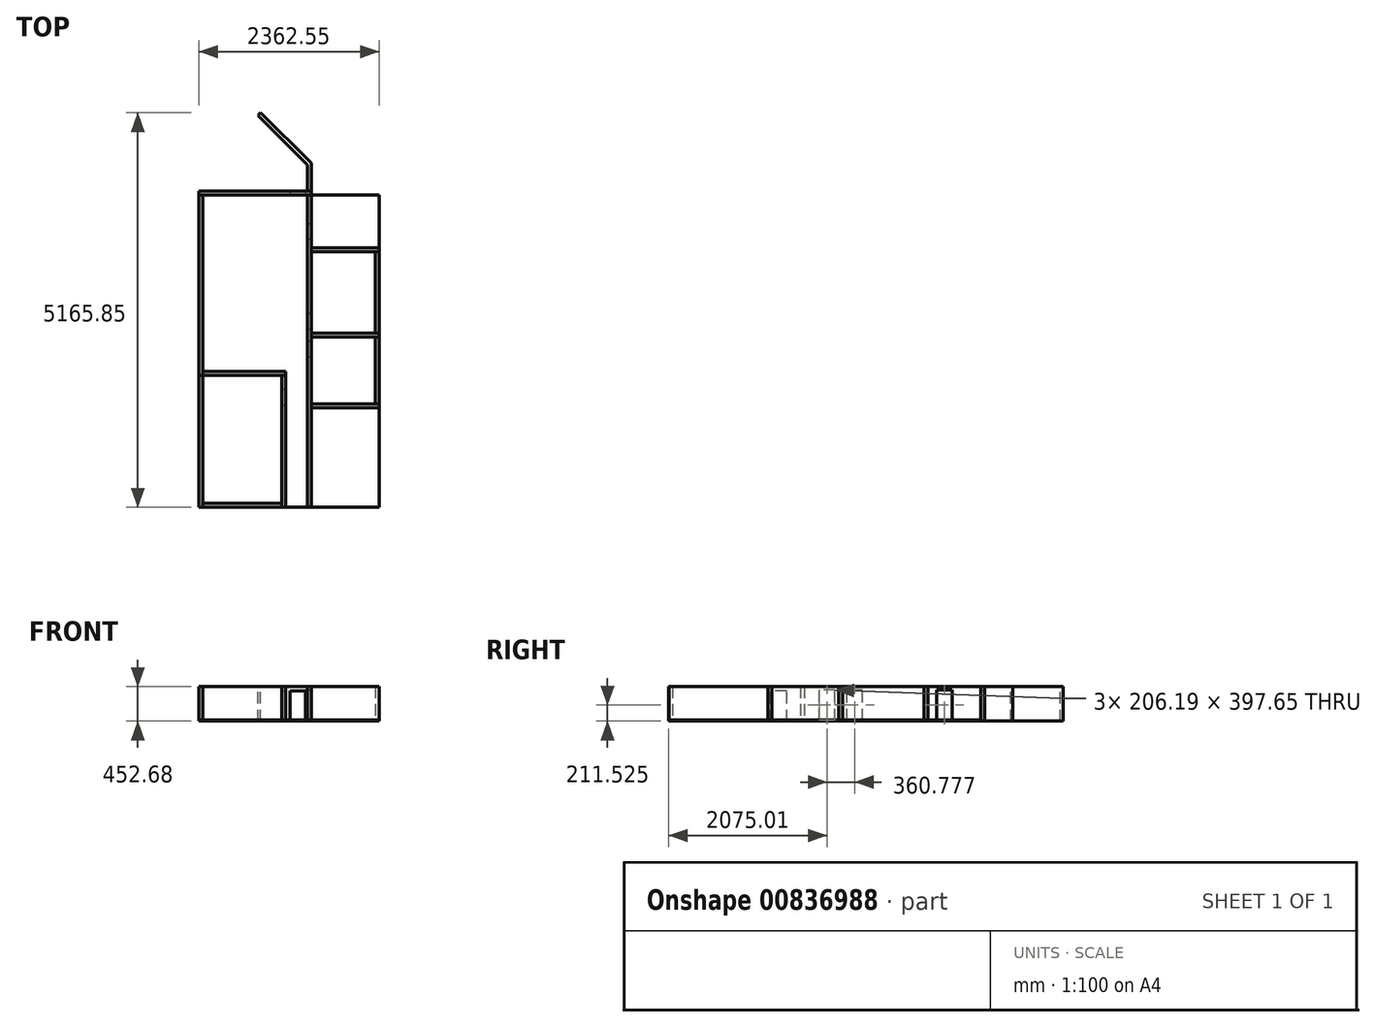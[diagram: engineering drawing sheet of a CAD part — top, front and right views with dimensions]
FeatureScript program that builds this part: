
annotation { "Feature Type Name" : "Feature", "Feature Type Description" : "" }
export const myFeature = defineFeature(function(context is Context, id is Id, definition is map)
    precondition{}
    {
        {
            var Q0;
            Q0=qCreatedBy(makeId("Front.planeOp"),FACE);
            var sketch = newSketch(context, id + "F0", { "sketchPlane" : qUnion([Q0])});
            skLineSegment(sketch, "E0.bottom", {"start": v(0, 0) * mm, "end": v(1473.55, 0) * mm});
            skLineSegment(sketch, "E0.top", {"start": v(0, 452.68) * mm, "end": v(1473.55, 452.68) * mm});
            skLineSegment(sketch, "E0.left", {"start": v(0, 0) * mm, "end": v(0, 452.68) * mm});
            skLineSegment(sketch, "E0.right", {"start": v(1473.55, 0) * mm, "end": v(1473.55, 452.68) * mm});
            skSolve(sketch);
        }
        {
            var Q0;
            Q0 = qSketchRegion(id + "F0", true);
            extrude(context, id + "F1", {"entities" : qUnion([Q0]), "depth" : 50.8 * mm, "offsetDistance" : 25.4 * mm});
        }
        {
            var Q0;
            Q0=makeQuery(id+"F1.opExtrude","CAP_FACE",FACE,{"disambiguationData":[OSD([sQuery(id+"F0.wireOp",EDGE,"E0.bottom"),sQuery(id+"F0.wireOp",EDGE,"E0.top"),sQuery(id+"F0.wireOp",EDGE,"E0.left"),sQuery(id+"F0.wireOp",EDGE,"E0.right")])],"isStart":false});
            var sketch = newSketch(context, id + "F2", { "sketchPlane" : qUnion([Q0])});
            skLineSegment(sketch, "E1.bottom", {"start": v(1397.99, 0) * mm, "end": v(1191.8, 0) * mm});
            skLineSegment(sketch, "E1.top", {"start": v(1397.99, 398.23) * mm, "end": v(1191.8, 398.23) * mm});
            skLineSegment(sketch, "E1.left", {"start": v(1397.99, 0) * mm, "end": v(1397.99, 398.23) * mm});
            skLineSegment(sketch, "E1.right", {"start": v(1191.8, 0) * mm, "end": v(1191.8, 398.23) * mm});
            skSolve(sketch);
        }
        {
            var Q0;
            Q0=makeQuery(id+"F2.imprint","IMPRINT",FACE,{"disambiguationData":[TD([[makeQuery(id+"F2.imprint","IMPRINT",EDGE,{"derivedFrom":sQuery(id+"F2.wireOp",EDGE,"E1.bottom")}),1.0]])]});
            extrude(context, id + "F3", {"entities" : qUnion([Q0]), "operationType" : NewBodyOperationType.REMOVE, "oppositeDirection" : true, "depth" : 71.12 * mm, "offsetDistance" : 25.4 * mm});
        }
        {
            var Q0;
            Q0=makeQuery(id+"F1.opExtrude","CAP_FACE",FACE,{"disambiguationData":[OSD([sQuery(id+"F0.wireOp",EDGE,"E0.bottom"),sQuery(id+"F0.wireOp",EDGE,"E0.top"),sQuery(id+"F0.wireOp",EDGE,"E0.left"),sQuery(id+"F0.wireOp",EDGE,"E0.right")])],"isStart":false});
            var sketch = newSketch(context, id + "F4", { "sketchPlane" : qUnion([Q0])});
            skLineSegment(sketch, "E2.bottom", {"start": v(0, 452.68) * mm, "end": v(50.8, 452.68) * mm});
            skLineSegment(sketch, "E2.top", {"start": v(0, 0) * mm, "end": v(50.8, 0) * mm});
            skLineSegment(sketch, "E2.left", {"start": v(0, 452.68) * mm, "end": v(0, 0) * mm});
            skLineSegment(sketch, "E2.right", {"start": v(50.8, 452.68) * mm, "end": v(50.8, 0) * mm});
            skSolve(sketch);
        }
        {
            var Q0;
            Q0=makeQuery(id+"F4.imprint","IMPRINT",FACE,{"disambiguationData":[TD([[makeQuery(id+"F4.imprint","IMPRINT",EDGE,{"derivedFrom":sQuery(id+"F4.wireOp",EDGE,"E2.bottom")}),-1.0]])]});
            extrude(context, id + "F5", {"entities" : qUnion([Q0]), "depth" : 2362.2 * mm, "offsetDistance" : 25.4 * mm});
        }
        {
            var Q0;
            Q0=makeQuery(id+"F5.opExtrude","SWEPT_FACE",FACE,{"disambiguationData":[OSD([sQuery(id+"F4.wireOp",EDGE,"E2.right")])]});
            var sketch = newSketch(context, id + "F6", { "sketchPlane" : qUnion([Q0])});
            skLineSegment(sketch, "E3.bottom", {"start": v(-2413, 452.68) * mm, "end": v(-2362.2, 452.68) * mm});
            skLineSegment(sketch, "E3.top", {"start": v(-2413, 0) * mm, "end": v(-2362.2, 0) * mm});
            skLineSegment(sketch, "E3.left", {"start": v(-2413, 452.68) * mm, "end": v(-2413, 0) * mm});
            skLineSegment(sketch, "E3.right", {"start": v(-2362.2, 452.68) * mm, "end": v(-2362.2, 0) * mm});
            skSolve(sketch);
        }
        {
            var Q0;
            Q0=makeQuery(id+"F6.imprint","IMPRINT",FACE,{"disambiguationData":[TD([[makeQuery(id+"F6.imprint","IMPRINT",EDGE,{"derivedFrom":sQuery(id+"F6.wireOp",EDGE,"E3.bottom")}),-1.0]])]});
            extrude(context, id + "F7", {"entities" : qUnion([Q0]), "depth" : 1084.58 * mm, "offsetDistance" : 25.4 * mm});
        }
        {
            var Q0;
            Q0=makeQuery(id+"F7.opExtrude","SWEPT_FACE",FACE,{"disambiguationData":[OSD([sQuery(id+"F6.wireOp",EDGE,"E3.left")])]});
            var sketch = newSketch(context, id + "F8", { "sketchPlane" : qUnion([Q0])});
            skLineSegment(sketch, "E4.bottom", {"start": v(1135.38, 452.68) * mm, "end": v(1084.58, 452.68) * mm});
            skLineSegment(sketch, "E4.top", {"start": v(1135.38, 0) * mm, "end": v(1084.58, 0) * mm});
            skLineSegment(sketch, "E4.left", {"start": v(1135.38, 452.68) * mm, "end": v(1135.38, 0) * mm});
            skLineSegment(sketch, "E4.right", {"start": v(1084.58, 452.68) * mm, "end": v(1084.58, 0) * mm});
            skSolve(sketch);
        }
        {
            var Q0;
            Q0=makeQuery(id+"F8.imprint","IMPRINT",FACE,{"disambiguationData":[TD([[makeQuery(id+"F8.imprint","IMPRINT",EDGE,{"derivedFrom":sQuery(id+"F8.wireOp",EDGE,"E4.bottom")}),1.0]])]});
            extrude(context, id + "F9", {"entities" : qUnion([Q0]), "depth" : 1727.2 * mm, "offsetDistance" : 25.4 * mm});
        }
        {
            var Q0;
            Q0=makeQuery(id+"F9.opExtrude","SWEPT_FACE",FACE,{"disambiguationData":[OSD([sQuery(id+"F8.wireOp",EDGE,"E4.left")])]});
            var sketch = newSketch(context, id + "F10", { "sketchPlane" : qUnion([Q0])});
            skLineSegment(sketch, "E5.bottom", {"start": v(-2593.9, 0) * mm, "end": v(-2800.09, 0) * mm});
            skLineSegment(sketch, "E5.top", {"start": v(-2593.9, 397.65) * mm, "end": v(-2800.09, 397.65) * mm});
            skLineSegment(sketch, "E5.left", {"start": v(-2593.9, 0) * mm, "end": v(-2593.9, 397.65) * mm});
            skLineSegment(sketch, "E5.right", {"start": v(-2800.09, 0) * mm, "end": v(-2800.09, 397.65) * mm});
            skSolve(sketch);
        }
        {
            var Q0;
            Q0=makeQuery(id+"F10.imprint","IMPRINT",FACE,{"disambiguationData":[TD([[makeQuery(id+"F10.imprint","IMPRINT",EDGE,{"derivedFrom":sQuery(id+"F10.wireOp",EDGE,"E5.bottom")}),1.0]])]});
            extrude(context, id + "F11", {"entities" : qUnion([Q0]), "operationType" : NewBodyOperationType.REMOVE, "oppositeDirection" : true, "depth" : 111.76 * mm, "offsetDistance" : 25.4 * mm});
        }
        {
            var Q0;
            Q0=makeQuery(id+"F1.opExtrude","CAP_FACE",FACE,{"disambiguationData":[OSD([sQuery(id+"F0.wireOp",EDGE,"E0.bottom"),sQuery(id+"F0.wireOp",EDGE,"E0.top"),sQuery(id+"F0.wireOp",EDGE,"E0.left"),sQuery(id+"F0.wireOp",EDGE,"E0.right")])],"isStart":false});
            var sketch = newSketch(context, id + "F12", { "sketchPlane" : qUnion([Q0])});
            skLineSegment(sketch, "E6.bottom", {"start": v(0, 0) * mm, "end": v(1473.55, 0) * mm});
            skLineSegment(sketch, "E6.top", {"start": v(0, 12.7) * mm, "end": v(1473.55, 12.7) * mm});
            skLineSegment(sketch, "E6.left", {"start": v(0, 0) * mm, "end": v(0, 12.7) * mm});
            skLineSegment(sketch, "E6.right", {"start": v(1473.55, 0) * mm, "end": v(1473.55, 12.7) * mm});
            skSolve(sketch);
        }
        {
            var Q0;
            {var subQ0=sQuery(id+"F12.wireOp",EDGE,"E6.left");Q0=makeQuery(id+"F12.imprint","IMPRINT",FACE,{"disambiguationData":[TD([[makeQuery(id+"F12.imprint","IMPRINT",EDGE,{"derivedFrom":subQ0}),-1.0]])]});}
            var Q1;
            {var subQ0=sQuery(id+"F12.wireOp",EDGE,"E6.bottom");var subQ1=makeQuery(id+"F3.boolean.opBoolean","COPY",EDGE,{"derivedFrom":makeQuery(id+"F3.opExtrude","CAP_EDGE",EDGE,{"disambiguationData":[OSD([sQuery(id+"F2.wireOp",EDGE,"E1.right")])],"isStart":true})});var subQ2=makeQuery(id+"F12.imprint","INTERSECT",VERTEX,{"derivedFrom":[subQ1,subQ0]});Q1=makeQuery(id+"F12.imprint","IMPRINT",FACE,{"disambiguationData":[TD([[makeQuery(id+"F12.imprint","IMPRINT",EDGE,{"disambiguationData":[TD([[subQ2,-1.0]])],"derivedFrom":subQ0}),1.0]])]});}
            var Q2;
            {var subQ0=sQuery(id+"F12.wireOp",EDGE,"E6.right");Q2=makeQuery(id+"F12.imprint","IMPRINT",FACE,{"disambiguationData":[TD([[makeQuery(id+"F12.imprint","IMPRINT",EDGE,{"derivedFrom":subQ0}),1.0]])]});}
            extrude(context, id + "F13", {"entities" : qUnion([Q0, Q1, Q2]), "depth" : 4089.4 * mm, "offsetDistance" : 25.4 * mm});
        }
        {
            var Q0;
            Q0=makeQuery(id+"F5.opExtrude","CAP_FACE",FACE,{"disambiguationData":[OSD([sQuery(id+"F4.wireOp",EDGE,"E2.bottom"),sQuery(id+"F4.wireOp",EDGE,"E2.top"),sQuery(id+"F4.wireOp",EDGE,"E2.left"),sQuery(id+"F4.wireOp",EDGE,"E2.right")])],"isStart":false});
            extrude(context, id + "F14", {"entities" : qUnion([Q0]), "depth" : 1727.2 * mm, "offsetDistance" : 25.4 * mm});
        }
        {
            var Q0;
            Q0=makeQuery(id+"F14.opExtrude","SWEPT_FACE",FACE,{"disambiguationData":[OSD([sQuery(id+"F4.wireOp",EDGE,"E2.right")])]});
            var sketch = newSketch(context, id + "F15", { "sketchPlane" : qUnion([Q0])});
            skLineSegment(sketch, "E7.bottom", {"start": v(-4140.2, 452.68) * mm, "end": v(-4089.4, 452.68) * mm});
            skLineSegment(sketch, "E7.top", {"start": v(-4140.2, 0) * mm, "end": v(-4089.4, 0) * mm});
            skLineSegment(sketch, "E7.left", {"start": v(-4140.2, 452.68) * mm, "end": v(-4140.2, 0) * mm});
            skLineSegment(sketch, "E7.right", {"start": v(-4089.4, 452.68) * mm, "end": v(-4089.4, 0) * mm});
            skSolve(sketch);
        }
        {
            var Q0;
            Q0=makeQuery(id+"F15.imprint","IMPRINT",FACE,{"disambiguationData":[TD([[makeQuery(id+"F15.imprint","IMPRINT",EDGE,{"derivedFrom":sQuery(id+"F15.wireOp",EDGE,"E7.bottom")}),-1.0]])]});
            extrude(context, id + "F16", {"entities" : qUnion([Q0]), "depth" : 1033.78 * mm, "offsetDistance" : 25.4 * mm});
        }
        {
            var Q0;
            Q0=makeQuery(id+"F1.opExtrude","CAP_FACE",FACE,{"disambiguationData":[OSD([sQuery(id+"F0.wireOp",EDGE,"E0.bottom"),sQuery(id+"F0.wireOp",EDGE,"E0.top"),sQuery(id+"F0.wireOp",EDGE,"E0.left"),sQuery(id+"F0.wireOp",EDGE,"E0.right")])],"isStart":false});
            var sketch = newSketch(context, id + "F17", { "sketchPlane" : qUnion([Q0])});
            skLineSegment(sketch, "E8.bottom", {"start": v(1473.55, 452.68) * mm, "end": v(1422.75, 452.68) * mm});
            skLineSegment(sketch, "E8.top", {"start": v(1473.55, 0) * mm, "end": v(1422.75, 0) * mm});
            skLineSegment(sketch, "E8.left", {"start": v(1473.55, 452.68) * mm, "end": v(1473.55, 0) * mm});
            skLineSegment(sketch, "E8.right", {"start": v(1422.75, 452.68) * mm, "end": v(1422.75, 0) * mm});
            skSolve(sketch);
        }
        {
            var Q0;
            Q0=makeQuery(id+"F17.imprint","IMPRINT",FACE,{"disambiguationData":[TD([[makeQuery(id+"F17.imprint","IMPRINT",EDGE,{"derivedFrom":sQuery(id+"F17.wireOp",EDGE,"E8.bottom")}),-1.0]])]});
            extrude(context, id + "F18", {"entities" : qUnion([Q0]), "depth" : 4081.78 * mm, "offsetDistance" : 25.4 * mm});
        }
        {
            var Q0;
            Q0=makeQuery(id+"F18.opExtrude","SWEPT_FACE",FACE,{"disambiguationData":[OSD([sQuery(id+"F17.wireOp",EDGE,"E8.left")])]});
            var sketch = newSketch(context, id + "F19", { "sketchPlane" : qUnion([Q0])});
            skLineSegment(sketch, "E9.bottom", {"start": v(-423.05, 12.7) * mm, "end": v(-629.23, 12.7) * mm});
            skLineSegment(sketch, "E9.top", {"start": v(-423.05, 410.35) * mm, "end": v(-629.23, 410.35) * mm});
            skLineSegment(sketch, "E9.left", {"start": v(-423.05, 12.7) * mm, "end": v(-423.05, 410.35) * mm});
            skLineSegment(sketch, "E9.right", {"start": v(-629.23, 12.7) * mm, "end": v(-629.23, 410.35) * mm});
            skLineSegment(sketch, "E10.bottom", {"start": v(-1601.32, 12.7) * mm, "end": v(-1807.5, 12.7) * mm});
            skLineSegment(sketch, "E10.top", {"start": v(-1601.32, 410.35) * mm, "end": v(-1807.5, 410.35) * mm});
            skLineSegment(sketch, "E10.left", {"start": v(-1601.32, 12.7) * mm, "end": v(-1601.32, 410.35) * mm});
            skLineSegment(sketch, "E10.right", {"start": v(-1807.5, 12.7) * mm, "end": v(-1807.5, 410.35) * mm});
            skLineSegment(sketch, "E11.bottom", {"start": v(-1962.1, 12.7) * mm, "end": v(-2168.29, 12.7) * mm});
            skLineSegment(sketch, "E11.top", {"start": v(-1962.1, 410.35) * mm, "end": v(-2168.29, 410.35) * mm});
            skLineSegment(sketch, "E11.left", {"start": v(-1962.1, 12.7) * mm, "end": v(-1962.1, 410.35) * mm});
            skLineSegment(sketch, "E11.right", {"start": v(-2168.29, 12.7) * mm, "end": v(-2168.29, 410.35) * mm});
            skSolve(sketch);
        }
        {
            var Q0;
            Q0=makeQuery(id+"F19.imprint","IMPRINT",FACE,{"disambiguationData":[TD([[makeQuery(id+"F19.imprint","IMPRINT",EDGE,{"derivedFrom":sQuery(id+"F19.wireOp",EDGE,"E11.bottom")}),-1.0]])]});
            var Q1;
            Q1=makeQuery(id+"F19.imprint","IMPRINT",FACE,{"disambiguationData":[TD([[makeQuery(id+"F19.imprint","IMPRINT",EDGE,{"derivedFrom":sQuery(id+"F19.wireOp",EDGE,"E10.bottom")}),-1.0]])]});
            var Q2;
            Q2=makeQuery(id+"F19.imprint","IMPRINT",FACE,{"disambiguationData":[TD([[makeQuery(id+"F19.imprint","IMPRINT",EDGE,{"derivedFrom":sQuery(id+"F19.wireOp",EDGE,"E9.bottom")}),-1.0]])]});
            extrude(context, id + "F20", {"entities" : qUnion([Q0, Q1, Q2]), "operationType" : NewBodyOperationType.REMOVE, "oppositeDirection" : true, "depth" : 314.96 * mm, "offsetDistance" : 25.4 * mm});
        }
        {
            var Q0;
            Q0=makeQuery(id+"F18.opExtrude","SWEPT_FACE",FACE,{"disambiguationData":[OSD([sQuery(id+"F17.wireOp",EDGE,"E8.left")])]});
            var sketch = newSketch(context, id + "F21", { "sketchPlane" : qUnion([Q0])});
            skLineSegment(sketch, "E12.bottom", {"start": v(-1910.2, 452.68) * mm, "end": v(-1859.4, 452.68) * mm});
            skLineSegment(sketch, "E12.top", {"start": v(-1910.2, 12.7) * mm, "end": v(-1859.4, 12.7) * mm});
            skLineSegment(sketch, "E12.left", {"start": v(-1910.2, 452.68) * mm, "end": v(-1910.2, 12.7) * mm});
            skLineSegment(sketch, "E12.right", {"start": v(-1859.4, 452.68) * mm, "end": v(-1859.4, 12.7) * mm});
            skSolve(sketch);
        }
        {
            var Q0;
            Q0=makeQuery(id+"F21.imprint","IMPRINT",FACE,{"disambiguationData":[TD([[makeQuery(id+"F21.imprint","IMPRINT",EDGE,{"derivedFrom":sQuery(id+"F21.wireOp",EDGE,"E12.bottom")}),-1.0]])]});
            extrude(context, id + "F22", {"entities" : qUnion([Q0]), "depth" : 889 * mm, "offsetDistance" : 25.4 * mm});
        }
        {
            var Q0;
            Q0=makeQuery(id+"F18.opExtrude","SWEPT_FACE",FACE,{"disambiguationData":[OSD([sQuery(id+"F17.wireOp",EDGE,"E8.left")])]});
            var sketch = newSketch(context, id + "F23", { "sketchPlane" : qUnion([Q0])});
            skLineSegment(sketch, "E13.bottom", {"start": v(-2840.54, 452.68) * mm, "end": v(-2789.74, 452.68) * mm});
            skLineSegment(sketch, "E13.top", {"start": v(-2840.54, 12.7) * mm, "end": v(-2789.74, 12.7) * mm});
            skLineSegment(sketch, "E13.left", {"start": v(-2840.54, 452.68) * mm, "end": v(-2840.54, 12.7) * mm});
            skLineSegment(sketch, "E13.right", {"start": v(-2789.74, 452.68) * mm, "end": v(-2789.74, 12.7) * mm});
            skSolve(sketch);
        }
        {
            var Q0;
            Q0=makeQuery(id+"F23.imprint","IMPRINT",FACE,{"disambiguationData":[TD([[makeQuery(id+"F23.imprint","IMPRINT",EDGE,{"derivedFrom":sQuery(id+"F23.wireOp",EDGE,"E13.bottom")}),-1.0]])]});
            extrude(context, id + "F24", {"entities" : qUnion([Q0]), "depth" : 889 * mm, "offsetDistance" : 25.4 * mm});
        }
        {
            var Q0;
            Q0=makeQuery(id+"F24.opExtrude","SWEPT_FACE",FACE,{"disambiguationData":[OSD([sQuery(id+"F23.wireOp",EDGE,"E13.right")])]});
            var sketch = newSketch(context, id + "F25", { "sketchPlane" : qUnion([Q0])});
            skLineSegment(sketch, "E14.bottom", {"start": v(-2362.55, 452.68) * mm, "end": v(-2311.75, 452.68) * mm});
            skLineSegment(sketch, "E14.top", {"start": v(-2362.55, 12.7) * mm, "end": v(-2311.75, 12.7) * mm});
            skLineSegment(sketch, "E14.left", {"start": v(-2362.55, 452.68) * mm, "end": v(-2362.55, 12.7) * mm});
            skLineSegment(sketch, "E14.right", {"start": v(-2311.75, 452.68) * mm, "end": v(-2311.75, 12.7) * mm});
            skSolve(sketch);
        }
        {
            var Q0;
            Q0=makeQuery(id+"F25.imprint","IMPRINT",FACE,{"disambiguationData":[TD([[makeQuery(id+"F25.imprint","IMPRINT",EDGE,{"derivedFrom":sQuery(id+"F25.wireOp",EDGE,"E14.bottom")}),-1.0]])]});
            extrude(context, id + "F26", {"entities" : qUnion([Q0]), "depth" : 879.53 * mm, "offsetDistance" : 25.4 * mm});
        }
        {
            var Q0;
            Q0=makeQuery(id+"F18.opExtrude","SWEPT_FACE",FACE,{"disambiguationData":[OSD([sQuery(id+"F17.wireOp",EDGE,"E8.left")])]});
            var sketch = newSketch(context, id + "F27", { "sketchPlane" : qUnion([Q0])});
            skLineSegment(sketch, "E15.bottom", {"start": v(-792.8, 452.68) * mm, "end": v(-742, 452.68) * mm});
            skLineSegment(sketch, "E15.top", {"start": v(-792.8, 12.7) * mm, "end": v(-742, 12.7) * mm});
            skLineSegment(sketch, "E15.left", {"start": v(-792.8, 452.68) * mm, "end": v(-792.8, 12.7) * mm});
            skLineSegment(sketch, "E15.right", {"start": v(-742, 452.68) * mm, "end": v(-742, 12.7) * mm});
            skSolve(sketch);
        }
        {
            var Q0;
            Q0=makeQuery(id+"F27.imprint","IMPRINT",FACE,{"disambiguationData":[TD([[makeQuery(id+"F27.imprint","IMPRINT",EDGE,{"derivedFrom":sQuery(id+"F27.wireOp",EDGE,"E15.bottom")}),-1.0]])]});
            extrude(context, id + "F28", {"entities" : qUnion([Q0]), "depth" : 889 * mm, "offsetDistance" : 25.4 * mm});
        }
        {
            var Q0;
            Q0=makeQuery(id+"F22.opExtrude","SWEPT_FACE",FACE,{"disambiguationData":[OSD([sQuery(id+"F21.wireOp",EDGE,"E12.right")])]});
            var sketch = newSketch(context, id + "F29", { "sketchPlane" : qUnion([Q0])});
            skLineSegment(sketch, "E16.bottom", {"start": v(-2362.55, 452.68) * mm, "end": v(-2311.75, 452.68) * mm});
            skLineSegment(sketch, "E16.top", {"start": v(-2362.55, 12.7) * mm, "end": v(-2311.75, 12.7) * mm});
            skLineSegment(sketch, "E16.left", {"start": v(-2362.55, 452.68) * mm, "end": v(-2362.55, 12.7) * mm});
            skLineSegment(sketch, "E16.right", {"start": v(-2311.75, 452.68) * mm, "end": v(-2311.75, 12.7) * mm});
            skSolve(sketch);
        }
        {
            var Q0;
            Q0=makeQuery(id+"F29.imprint","IMPRINT",FACE,{"disambiguationData":[TD([[makeQuery(id+"F29.imprint","IMPRINT",EDGE,{"derivedFrom":sQuery(id+"F29.wireOp",EDGE,"E16.bottom")}),-1.0]])]});
            extrude(context, id + "F30", {"entities" : qUnion([Q0]), "depth" : 1066.6 * mm, "offsetDistance" : 25.4 * mm});
        }
        {
            var Q0;
            Q0=makeQuery(id+"F13.opExtrude","SWEPT_FACE",FACE,{"disambiguationData":[OSD([sQuery(id+"F12.wireOp",EDGE,"E6.right")])]});
            extrude(context, id + "F31", {"entities" : qUnion([Q0]), "depth" : 889 * mm, "offsetDistance" : 25.4 * mm});
        }
        {
            var Q0;
            Q0=makeQuery(id+"F1.opExtrude","CAP_FACE",FACE,{"disambiguationData":[OSD([sQuery(id+"F0.wireOp",EDGE,"E0.bottom"),sQuery(id+"F0.wireOp",EDGE,"E0.top"),sQuery(id+"F0.wireOp",EDGE,"E0.left"),sQuery(id+"F0.wireOp",EDGE,"E0.right")])],"isStart":true});
            var sketch = newSketch(context, id + "F32", { "sketchPlane" : qUnion([Q0])});
            skLineSegment(sketch, "E17.bottom", {"start": v(-1473.55, 452.68) * mm, "end": v(-1422.75, 452.68) * mm});
            skLineSegment(sketch, "E17.top", {"start": v(-1473.55, 0) * mm, "end": v(-1422.75, 0) * mm});
            skLineSegment(sketch, "E17.left", {"start": v(-1473.55, 452.68) * mm, "end": v(-1473.55, 0) * mm});
            skLineSegment(sketch, "E17.right", {"start": v(-1422.75, 452.68) * mm, "end": v(-1422.75, 0) * mm});
            skSolve(sketch);
        }
        {
            var Q0;
            Q0=makeQuery(id+"F32.imprint","IMPRINT",FACE,{"disambiguationData":[TD([[makeQuery(id+"F32.imprint","IMPRINT",EDGE,{"derivedFrom":sQuery(id+"F32.wireOp",EDGE,"E17.bottom")}),1.0]])]});
            extrude(context, id + "F33", {"entities" : qUnion([Q0]), "depth" : 381 * mm, "offsetDistance" : 25.4 * mm});
        }
        {
            var Q0;
            Q0=makeQuery(id+"F33.opExtrude","SWEPT_FACE",FACE,{"disambiguationData":[OSD([sQuery(id+"F32.wireOp",EDGE,"E17.bottom")])]});
            var sketch = newSketch(context, id + "F34", { "sketchPlane" : qUnion([Q0])});
            skLineSegment(sketch, "E18", {"start": v(1422.75, 381) * mm, "end": v(1422.75, 344.97) * mm});
            skLineSegment(sketch, "E19", {"start": v(1422.75, 344.97) * mm, "end": v(1458.56, 381) * mm});
            skLineSegment(sketch, "E20", {"start": v(1458.56, 381) * mm, "end": v(1422.75, 381) * mm});
            skSolve(sketch);
        }
        {
            var Q0;
            Q0=makeQuery(id+"F34.imprint","IMPRINT",FACE,{"disambiguationData":[TD([[makeQuery(id+"F34.imprint","IMPRINT",EDGE,{"derivedFrom":sQuery(id+"F34.wireOp",EDGE,"E18")}),1.0]])]});
            extrude(context, id + "F35", {"entities" : qUnion([Q0]), "operationType" : NewBodyOperationType.REMOVE, "oppositeDirection" : true, "depth" : 505.46 * mm, "offsetDistance" : 25.4 * mm});
        }
        {
            var Q0;
            Q0=makeQuery(id+"F35.boolean.opBoolean","COPY",FACE,{"derivedFrom":makeQuery(id+"F35.opExtrude","SWEPT_FACE",FACE,{"disambiguationData":[OSD([sQuery(id+"F34.wireOp",EDGE,"E19")])]})});
            extrude(context, id + "F36", {"entities" : qUnion([Q0]), "operationType" : NewBodyOperationType.ADD, "depth" : 914.4 * mm, "offsetDistance" : 25.4 * mm});
        }
        {
            var Q0;
            Q0=makeQuery(id+"F36.boolean.opBoolean","MERGE",FACE,{"derivedFrom":[makeQuery(id+"F33.opExtrude","SWEPT_FACE",FACE,{"disambiguationData":[OSD([sQuery(id+"F32.wireOp",EDGE,"E17.bottom")])]}),makeQuery(id+"F36.opExtrude","SWEPT_FACE",FACE,{"disambiguationData":[OSD([sQuery(id+"F34.wireOp",EDGE,"E19")])]})]});
            var sketch = newSketch(context, id + "F37", { "sketchPlane" : qUnion([Q0])});
            skLineSegment(sketch, "E21", {"start": v(1458.56, 381) * mm, "end": v(1473.55, 366.1) * mm});
            skLineSegment(sketch, "E22", {"start": v(1473.55, 366.1) * mm, "end": v(1473.55, 381) * mm});
            skLineSegment(sketch, "E23", {"start": v(1473.55, 381) * mm, "end": v(1458.56, 381) * mm});
            skSolve(sketch);
        }
        {
            var Q0;
            Q0=makeQuery(id+"F37.imprint","IMPRINT",FACE,{"disambiguationData":[TD([[makeQuery(id+"F37.imprint","IMPRINT",EDGE,{"derivedFrom":sQuery(id+"F37.wireOp",EDGE,"E21")}),1.0]])]});
            extrude(context, id + "F38", {"entities" : qUnion([Q0]), "operationType" : NewBodyOperationType.REMOVE, "oppositeDirection" : true, "depth" : 546.1 * mm, "offsetDistance" : 25.4 * mm});
        }
    });
